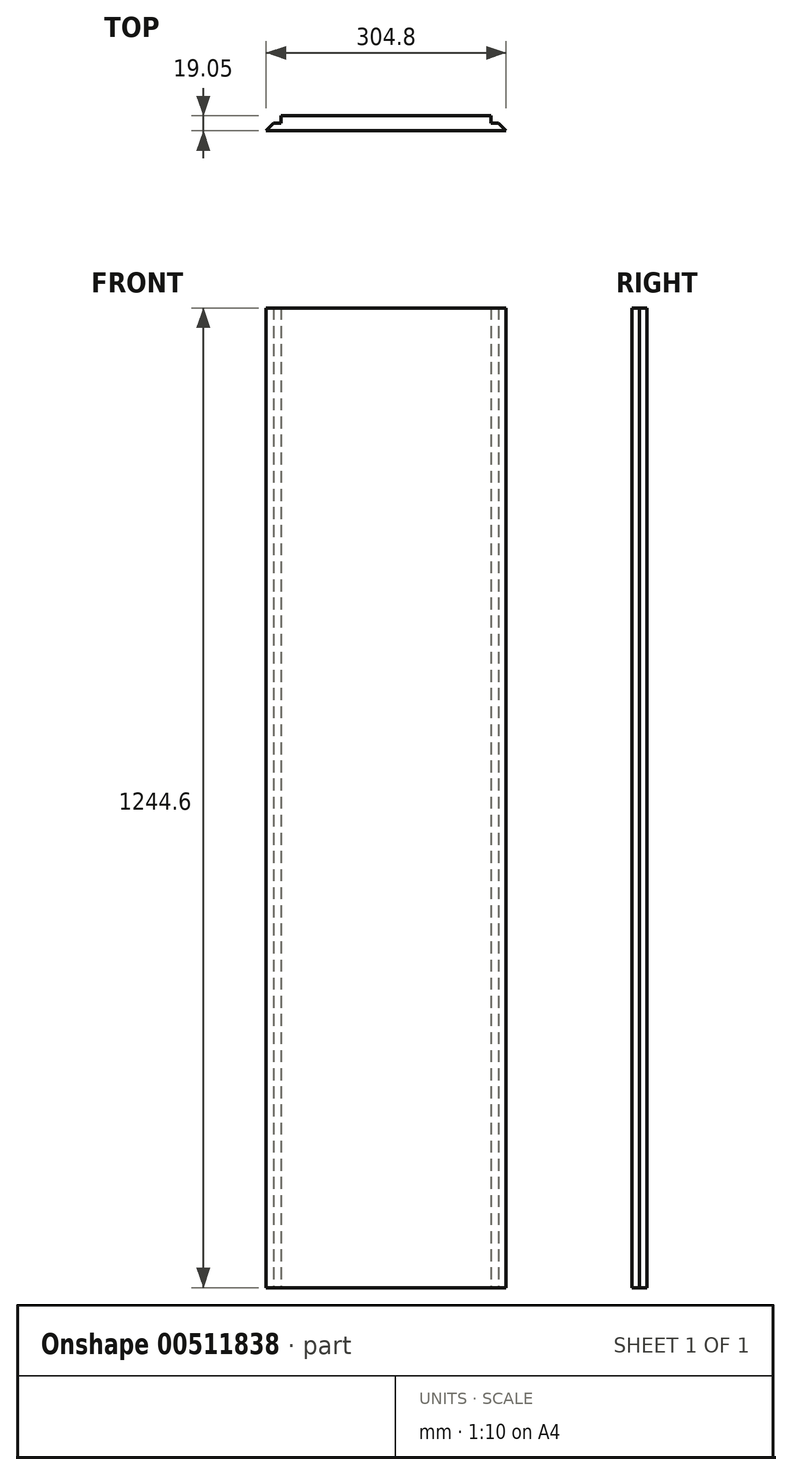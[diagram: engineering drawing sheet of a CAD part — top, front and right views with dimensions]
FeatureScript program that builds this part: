
annotation { "Feature Type Name" : "Feature", "Feature Type Description" : "" }
export const myFeature = defineFeature(function(context is Context, id is Id, definition is map)
    precondition{}
    {
        {
            var Q0;
            Q0=qCreatedBy(makeId("Top.planeOp"),FACE);
            var sketch = newSketch(context, id + "F0", { "sketchPlane" : qUnion([Q0])});
            skLineSegment(sketch, "E0.bottom", {"start": v(-266.4, -17.55) * mm, "end": v(38.4, -17.55) * mm});
            skLineSegment(sketch, "E0.top", {"start": v(-266.4, -36.6) * mm, "end": v(38.4, -36.6) * mm});
            skLineSegment(sketch, "E0.left", {"start": v(-266.4, -17.55) * mm, "end": v(-266.4, -36.6) * mm});
            skLineSegment(sketch, "E0.right", {"start": v(38.4, -17.55) * mm, "end": v(38.4, -36.6) * mm});
            skLineSegment(sketch, "E1", {"start": v(-266.4, -36.6) * mm, "end": v(-256.87, -27.08) * mm});
            skPoint(sketch, "E1.endSnap0", {"position": v(-266.4, -27.08) * mm});
            skLineSegment(sketch, "E2", {"start": v(-256.87, -27.08) * mm, "end": v(-247.35, -27.08) * mm});
            skLineSegment(sketch, "E3", {"start": v(-247.35, -27.08) * mm, "end": v(-247.35, -17.55) * mm});
            skLineSegment(sketch, "E4", {"start": v(-114, -17.55) * mm, "end": v(-114, -36.6) * mm, "construction": true});
            skLineSegment(sketch, "E5.MirrorCS", {"start": v(19.35, -27.08) * mm, "end": v(19.35, -17.55) * mm});
            skLineSegment(sketch, "E6.MirrorCS", {"start": v(28.88, -27.08) * mm, "end": v(19.35, -27.08) * mm});
            skLineSegment(sketch, "E7.MirrorCS", {"start": v(38.4, -36.6) * mm, "end": v(28.88, -27.08) * mm});
            skLineSegment(sketch, "E8.MirrorCS", {"start": v(38.4, -17.55) * mm, "end": v(-266.4, -17.55) * mm});
            skLineSegment(sketch, "E9", {"start": v(-247.35, -27.08) * mm, "end": v(19.35, -27.08) * mm});
            skSolve(sketch);
        }
        {
            var Q0;
            {var subQ0=sQuery(id+"F0.wireOp",EDGE,"E3");Q0=makeQuery(id+"F0.imprint","IMPRINT",FACE,{"disambiguationData":[TD([[makeQuery(id+"F0.imprint","IMPRINT",EDGE,{"derivedFrom":subQ0}),-1.0]])]});}
            var Q1;
            Q1=makeQuery(id+"F0.imprint","IMPRINT",FACE,{"disambiguationData":[TD([[makeQuery(id+"F0.imprint","IMPRINT",EDGE,{"derivedFrom":sQuery(id+"F0.wireOp",EDGE,"E0.top")}),1.0]])]});
            extrude(context, id + "F1", {"entities" : qUnion([Q0, Q1]), "depth" : 1244.6 * mm, "offsetDistance" : 25.4 * mm});
        }
    });
